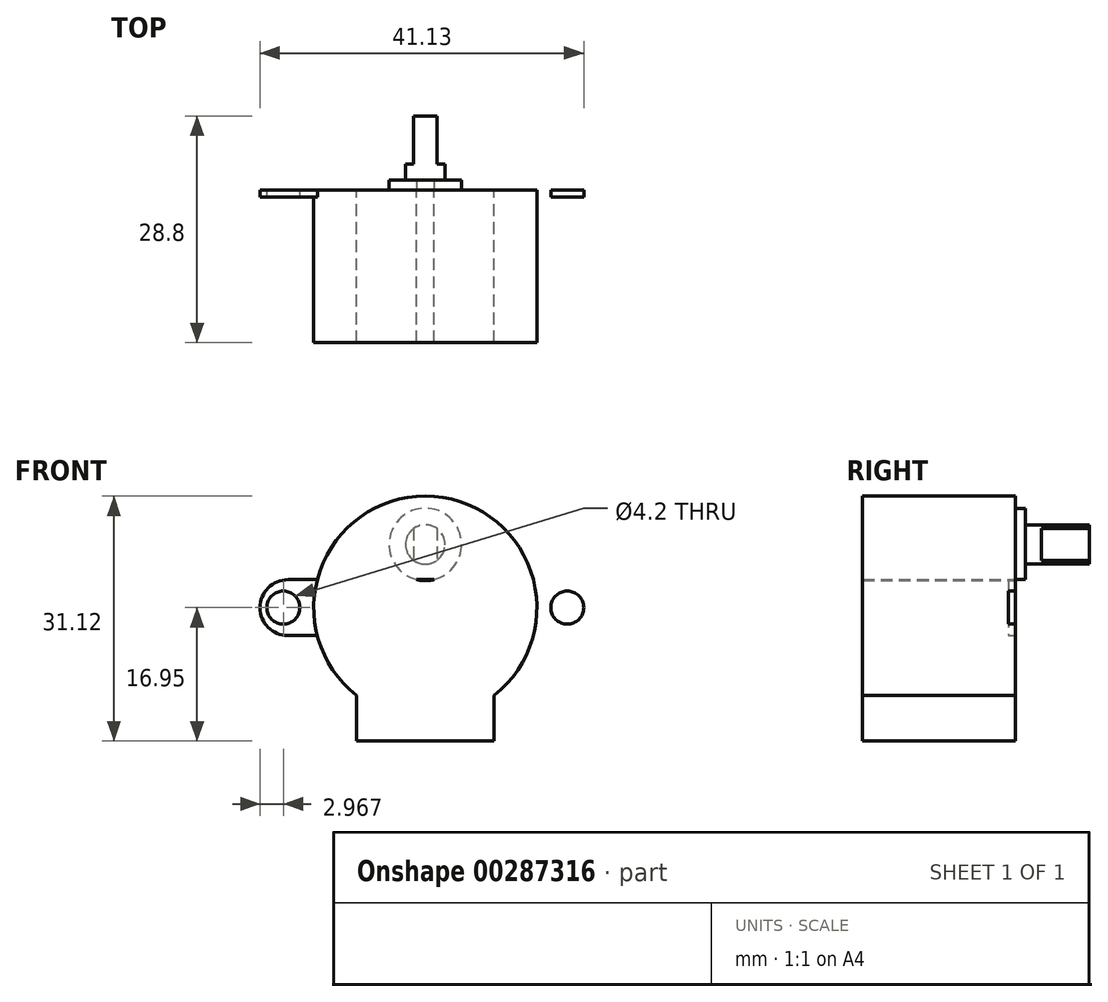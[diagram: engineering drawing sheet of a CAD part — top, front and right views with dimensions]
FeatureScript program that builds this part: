
annotation { "Feature Type Name" : "Feature", "Feature Type Description" : "" }
export const myFeature = defineFeature(function(context is Context, id is Id, definition is map)
    precondition{}
    {
        {
            var Q0;
            Q0=qCreatedBy(makeId("Front.planeOp"),FACE);
            var sketch = newSketch(context, id + "F0", { "sketchPlane" : qUnion([Q0])});
            skCircle(sketch, "E0", {"center": v(0, 0) * mm, "radius": 14.17 * mm});
            skLineSegment(sketch, "E1.bottom", {"start": v(8.75, -16.95) * mm, "end": v(-8.75, -16.95) * mm});
            skLineSegment(sketch, "E1.top", {"start": v(8.75, -11.15) * mm, "end": v(-8.75, -11.15) * mm});
            skLineSegment(sketch, "E1.left", {"start": v(8.75, -16.95) * mm, "end": v(8.75, -11.15) * mm});
            skLineSegment(sketch, "E1.right", {"start": v(-8.75, -16.95) * mm, "end": v(-8.75, -11.15) * mm});
            skPoint(sketch, "E1.middle", {"position": v(0, -14.05) * mm});
            skLineSegment(sketch, "E2.bottom", {"start": v(17.45, -3.55) * mm, "end": v(-17.45, -3.55) * mm});
            skLineSegment(sketch, "E2.top", {"start": v(17.45, 3.55) * mm, "end": v(-17.45, 3.55) * mm});
            skLineSegment(sketch, "E2.left", {"start": v(21, 0) * mm, "end": v(21, 0) * mm});
            skLineSegment(sketch, "E2.right", {"start": v(-21, 0) * mm, "end": v(-21, 0) * mm});
            skCircle(sketch, "E3", {"center": v(-18.03, 0) * mm, "radius": 2.1 * mm});
            skCircle(sketch, "E4.MirrorC", {"center": v(18.03, 0) * mm, "radius": 2.1 * mm});
            skPoint(sketch, "E5.visualSharp", {"position": v(21, 3.55) * mm});
            skArc(sketch, "E5.filletArc", {"start": v(21, 0) * mm, "mid": v(19.96, 2.51) * mm, "end": v(17.45, 3.55) * mm});
            skPoint(sketch, "E6.visualSharp", {"position": v(21, -3.55) * mm});
            skArc(sketch, "E6.filletArc", {"start": v(17.45, -3.55) * mm, "mid": v(19.96, -2.51) * mm, "end": v(21, 0) * mm});
            skPoint(sketch, "E7.visualSharp", {"position": v(-21, 3.55) * mm});
            skArc(sketch, "E7.filletArc", {"start": v(-17.45, 3.55) * mm, "mid": v(-19.96, 2.51) * mm, "end": v(-21, 0) * mm});
            skPoint(sketch, "E8.visualSharp", {"position": v(-21, -3.55) * mm});
            skArc(sketch, "E8.filletArc", {"start": v(-21, 0) * mm, "mid": v(-19.96, -2.51) * mm, "end": v(-17.45, -3.55) * mm});
            skCircle(sketch, "E9", {"center": v(0, 8.02) * mm, "radius": 4.6 * mm});
            skCircle(sketch, "E10", {"center": v(0, 8.02) * mm, "radius": 2.5 * mm});
            skLineSegment(sketch, "E11.0", {"start": v(-1.47, 10.04) * mm, "end": v(-1.47, 6) * mm});
            skLineSegment(sketch, "E12.0", {"start": v(1.48, 10.04) * mm, "end": v(1.48, 6) * mm});
            skSolve(sketch);
        }
        {
            var Q0;
            {var subQ0=sQuery(id+"F0.wireOp",EDGE,"E2.top");var subQ1=sQuery(id+"F0.wireOp",EDGE,"E0");var subQ2=makeQuery(id+"F0.imprint","INTERSECT",VERTEX,{"disambiguationData":[OD(0.0)],"derivedFrom":[subQ1,subQ0]});Q0=makeQuery(id+"F0.imprint","IMPRINT",FACE,{"disambiguationData":[TD([[makeQuery(id+"F0.imprint","IMPRINT",EDGE,{"disambiguationData":[TD([[subQ2,1.0]])],"derivedFrom":subQ1}),1.0]])]});}
            var Q1;
            {var subQ0=sQuery(id+"F0.wireOp",EDGE,"E2.top");var subQ1=sQuery(id+"F0.wireOp",EDGE,"E0");var subQ2=makeQuery(id+"F0.imprint","INTERSECT",VERTEX,{"disambiguationData":[OD(0.0)],"derivedFrom":[subQ1,subQ0]});Q1=makeQuery(id+"F0.imprint","IMPRINT",FACE,{"disambiguationData":[TD([[makeQuery(id+"F0.imprint","IMPRINT",EDGE,{"disambiguationData":[TD([[subQ2,-1.0]])],"derivedFrom":subQ1}),1.0]])]});}
            var Q2;
            {var subQ0=sQuery(id+"F0.wireOp",EDGE,"E1.top");Q2=makeQuery(id+"F0.imprint","IMPRINT",FACE,{"disambiguationData":[TD([[makeQuery(id+"F0.imprint","IMPRINT",EDGE,{"derivedFrom":subQ0}),-1.0]])]});}
            var Q3;
            Q3=makeQuery(id+"F0.imprint","IMPRINT",FACE,{"disambiguationData":[TD([[makeQuery(id+"F0.imprint","IMPRINT",EDGE,{"derivedFrom":sQuery(id+"F0.wireOp",EDGE,"E1.bottom")}),-1.0]])]});
            var Q4;
            {var subQ0=sQuery(id+"F0.wireOp",EDGE,"E1.top");Q4=makeQuery(id+"F0.imprint","IMPRINT",FACE,{"disambiguationData":[TD([[makeQuery(id+"F0.imprint","IMPRINT",EDGE,{"derivedFrom":subQ0}),1.0]])]});}
            var Q5;
            {var subQ6=sQuery(id+"F0.wireOp",EDGE,"E9");var subQ7=sQuery(id+"F0.wireOp",EDGE,"E2.top");var subQ8=makeQuery(id+"F0.imprint","INTERSECT",VERTEX,{"disambiguationData":[OD(0.0)],"derivedFrom":[subQ7,subQ6]});Q5=makeQuery(id+"F0.imprint","IMPRINT",FACE,{"disambiguationData":[TD([[makeQuery(id+"F0.imprint","IMPRINT",EDGE,{"disambiguationData":[TD([[subQ8,-1.0]])],"derivedFrom":subQ7}),-1.0]])]});}
            var Q6;
            {var subQ0=sQuery(id+"F0.wireOp",EDGE,"E11.0");Q6=makeQuery(id+"F0.imprint","IMPRINT",FACE,{"disambiguationData":[TD([[makeQuery(id+"F0.imprint","IMPRINT",EDGE,{"derivedFrom":subQ0}),1.0]])]});}
            var Q7;
            {var subQ0=sQuery(id+"F0.wireOp",EDGE,"E12.0");Q7=makeQuery(id+"F0.imprint","IMPRINT",FACE,{"disambiguationData":[TD([[makeQuery(id+"F0.imprint","IMPRINT",EDGE,{"derivedFrom":subQ0}),1.0]])]});}
            var Q8;
            {var subQ0=sQuery(id+"F0.wireOp",EDGE,"E11.0");Q8=makeQuery(id+"F0.imprint","IMPRINT",FACE,{"disambiguationData":[TD([[makeQuery(id+"F0.imprint","IMPRINT",EDGE,{"derivedFrom":subQ0}),-1.0]])]});}
            extrude(context, id + "F1", {"entities" : qUnion([Q0, Q1, Q2, Q3, Q4, Q5, Q6, Q7, Q8]), "depth" : 19.4 * mm});
        }
        {
            var Q0;
            Q0=makeQuery(id+"F0.imprint","IMPRINT",FACE,{"disambiguationData":[TD([[makeQuery(id+"F0.imprint","IMPRINT",EDGE,{"derivedFrom":sQuery(id+"F0.wireOp",EDGE,"E4.MirrorC")}),1.0]])]});
            var Q1;
            Q1=makeQuery(id+"F0.imprint","IMPRINT",FACE,{"disambiguationData":[TD([[makeQuery(id+"F0.imprint","IMPRINT",EDGE,{"derivedFrom":sQuery(id+"F0.wireOp",EDGE,"E3")}),-1.0]])]});
            extrude(context, id + "F2", {"entities" : qUnion([Q0, Q1]), "operationType" : NewBodyOperationType.ADD, "depth" : .9 * mm});
        }
        {
            var Q0;
            {var subQ6=sQuery(id+"F0.wireOp",EDGE,"E9");var subQ7=sQuery(id+"F0.wireOp",EDGE,"E2.top");var subQ8=makeQuery(id+"F0.imprint","INTERSECT",VERTEX,{"disambiguationData":[OD(0.0)],"derivedFrom":[subQ7,subQ6]});Q0=makeQuery(id+"F0.imprint","IMPRINT",FACE,{"disambiguationData":[TD([[makeQuery(id+"F0.imprint","IMPRINT",EDGE,{"disambiguationData":[TD([[subQ8,-1.0]])],"derivedFrom":subQ7}),-1.0]])]});}
            extrude(context, id + "F3", {"entities" : qUnion([Q0]), "operationType" : NewBodyOperationType.ADD, "oppositeDirection" : true, "depth" : 1.25 * mm});
        }
        {
            var Q0;
            {var subQ0=sQuery(id+"F0.wireOp",EDGE,"E11.0");Q0=makeQuery(id+"F0.imprint","IMPRINT",FACE,{"disambiguationData":[TD([[makeQuery(id+"F0.imprint","IMPRINT",EDGE,{"derivedFrom":subQ0}),-1.0]])]});}
            var Q1;
            {var subQ0=sQuery(id+"F0.wireOp",EDGE,"E11.0");Q1=makeQuery(id+"F0.imprint","IMPRINT",FACE,{"disambiguationData":[TD([[makeQuery(id+"F0.imprint","IMPRINT",EDGE,{"derivedFrom":subQ0}),1.0]])]});}
            var Q2;
            {var subQ0=sQuery(id+"F0.wireOp",EDGE,"E12.0");Q2=makeQuery(id+"F0.imprint","IMPRINT",FACE,{"disambiguationData":[TD([[makeQuery(id+"F0.imprint","IMPRINT",EDGE,{"derivedFrom":subQ0}),1.0]])]});}
            extrude(context, id + "F4", {"entities" : qUnion([Q0, Q1, Q2]), "operationType" : NewBodyOperationType.ADD, "oppositeDirection" : true, "depth" : 3.3 * mm});
        }
        {
            var Q0;
            {var subQ0=sQuery(id+"F0.wireOp",EDGE,"E11.0");Q0=makeQuery(id+"F0.imprint","IMPRINT",FACE,{"disambiguationData":[TD([[makeQuery(id+"F0.imprint","IMPRINT",EDGE,{"derivedFrom":subQ0}),1.0]])]});}
            extrude(context, id + "F5", {"entities" : qUnion([Q0]), "operationType" : NewBodyOperationType.ADD, "oppositeDirection" : true, "depth" : 9.4 * mm});
        }
    });
